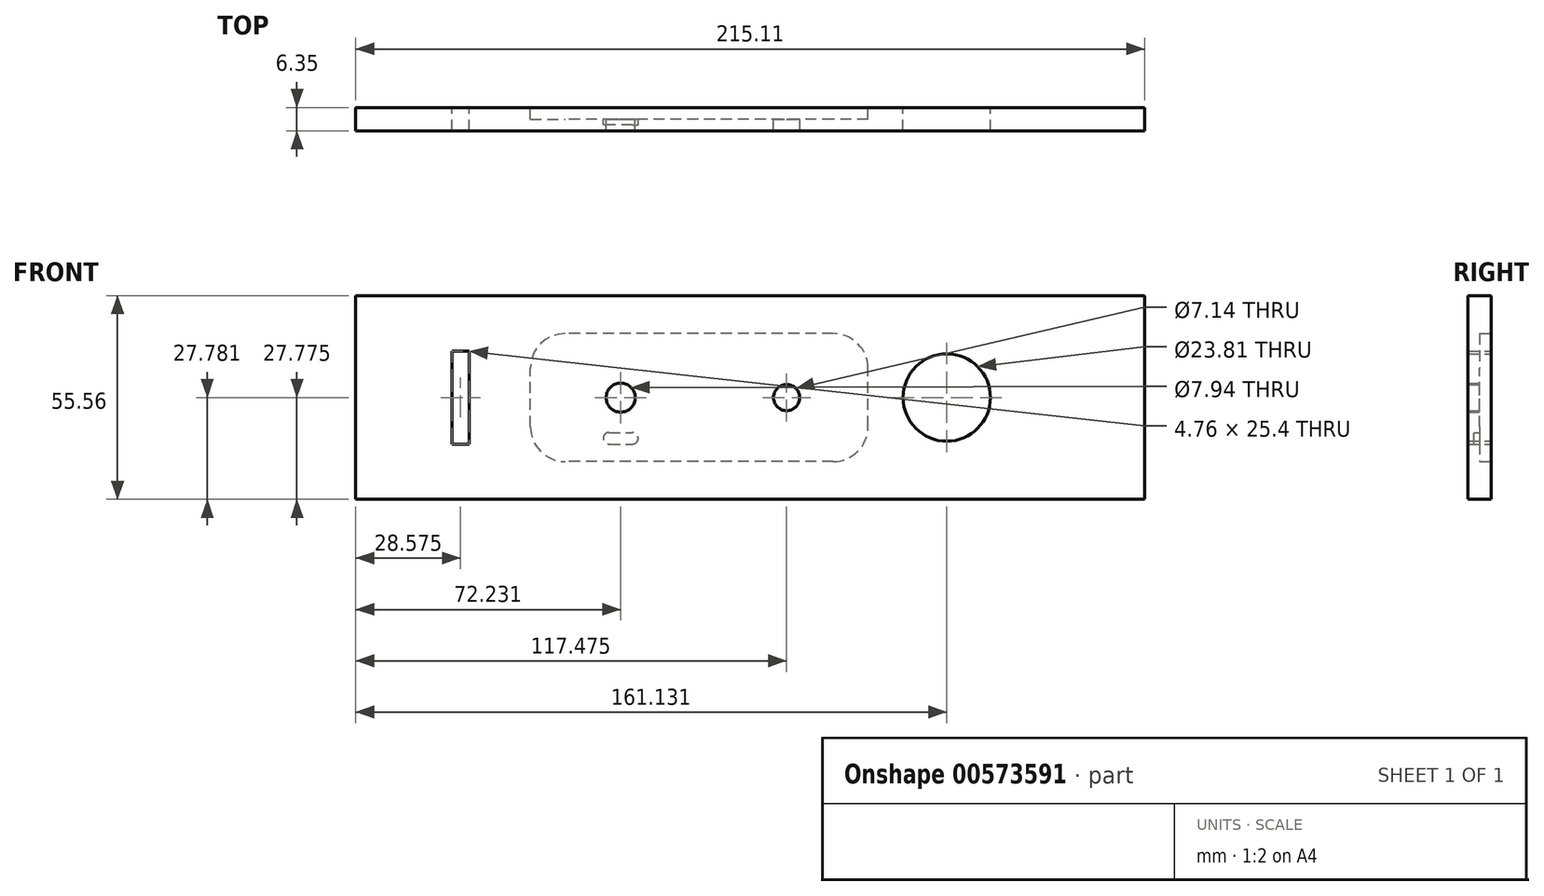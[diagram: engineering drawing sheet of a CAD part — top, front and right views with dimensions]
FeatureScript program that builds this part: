
annotation { "Feature Type Name" : "Feature", "Feature Type Description" : "" }
export const myFeature = defineFeature(function(context is Context, id is Id, definition is map)
    precondition{}
    {
        {
            var Q0;
            Q0=qCreatedBy(makeId("Front.planeOp"),FACE);
            var sketch = newSketch(context, id + "F0", { "sketchPlane" : qUnion([Q0])});
            skLineSegment(sketch, "E0.bottom", {"start": v(215.1, 55.56) * mm, "end": v(0, 55.56) * mm});
            skLineSegment(sketch, "E0.top", {"start": v(215.1, 0) * mm, "end": v(0, 0) * mm});
            skLineSegment(sketch, "E0.left", {"start": v(215.1, 55.56) * mm, "end": v(215.1, 0) * mm});
            skLineSegment(sketch, "E0.right", {"start": v(0, 55.56) * mm, "end": v(0, 0) * mm});
            skCircle(sketch, "E1", {"center": v(161.13, 27.78) * mm, "radius": 11.9 * mm});
            skCircle(sketch, "E2", {"center": v(117.48, 27.78) * mm, "radius": 3.57 * mm});
            skCircle(sketch, "E3", {"center": v(72.23, 27.77) * mm, "radius": 3.97 * mm});
            skSolve(sketch);
        }
        {
            var Q0;
            Q0 = qSketchRegion(id + "F0", true);
            extrude(context, id + "F1", {"entities" : qUnion([Q0]), "depth" : 6.35 * mm, "offsetDistance" : 25.4 * mm});
        }
        {
            var Q0;
            Q0=makeQuery(id+"F1.opExtrude","CAP_FACE",FACE,{"disambiguationData":[OSD([sQuery(id+"F0.wireOp",EDGE,"E0.bottom"),sQuery(id+"F0.wireOp",EDGE,"E0.top"),sQuery(id+"F0.wireOp",EDGE,"E0.left"),sQuery(id+"F0.wireOp",EDGE,"E0.right"),sQuery(id+"F0.wireOp",EDGE,"E1"),sQuery(id+"F0.wireOp",EDGE,"E2"),sQuery(id+"F0.wireOp",EDGE,"E3")])],"isStart":false});
            var sketch = newSketch(context, id + "F2", { "sketchPlane" : qUnion([Q0])});
            skLineSegment(sketch, "E4.bottom", {"start": v(26.2, 15.08) * mm, "end": v(30.96, 15.08) * mm});
            skLineSegment(sketch, "E4.top", {"start": v(26.2, 40.48) * mm, "end": v(30.96, 40.48) * mm});
            skLineSegment(sketch, "E4.left", {"start": v(26.2, 15.08) * mm, "end": v(26.2, 40.48) * mm});
            skLineSegment(sketch, "E4.right", {"start": v(30.96, 15.08) * mm, "end": v(30.96, 40.48) * mm});
            skSolve(sketch);
        }
        {
            var Q0;
            Q0 = qSketchRegion(id + "F2", true);
            extrude(context, id + "F3", {"entities" : qUnion([Q0]), "operationType" : NewBodyOperationType.REMOVE, "endBound" : BoundingType.THROUGH_ALL, "depth" : 25.4 * mm, "offsetDistance" : 25.4 * mm, "hasSecondDirection" : true, "secondDirectionBound" : SecondDirectionBoundingType.THROUGH_ALL, "secondDirectionOppositeDirection" : true, "secondDirectionDepth" : 25.4 * mm});
        }
        {
            var Q0;
            Q0=makeQuery(id+"F0.imprint","IMPRINT",FACE,{"disambiguationData":[TD([[makeQuery(id+"F0.imprint","IMPRINT",EDGE,{"derivedFrom":sQuery(id+"F0.wireOp",EDGE,"E0.bottom")}),1.0]])]});
            var sketch = newSketch(context, id + "F4", { "sketchPlane" : qUnion([Q0])});
            skLineSegment(sketch, "E5.bottom", {"start": v(130.18, 10.31) * mm, "end": v(57.15, 10.31) * mm});
            skLineSegment(sketch, "E5.top", {"start": v(130.18, 45.24) * mm, "end": v(57.15, 45.24) * mm});
            skLineSegment(sketch, "E5.left", {"start": v(139.7, 19.84) * mm, "end": v(139.7, 35.71) * mm});
            skLineSegment(sketch, "E5.right", {"start": v(47.63, 19.84) * mm, "end": v(47.63, 35.71) * mm});
            skPoint(sketch, "E6.visualSharp", {"position": v(139.7, 45.24) * mm});
            skArc(sketch, "E6.filletArc", {"start": v(139.7, 35.71) * mm, "mid": v(136.91, 42.45) * mm, "end": v(130.18, 45.24) * mm});
            skPoint(sketch, "E7.visualSharp", {"position": v(139.7, 10.31) * mm});
            skArc(sketch, "E7.filletArc", {"start": v(130.18, 10.31) * mm, "mid": v(136.91, 13.1) * mm, "end": v(139.7, 19.84) * mm});
            skPoint(sketch, "E8.visualSharp", {"position": v(47.63, 10.31) * mm});
            skArc(sketch, "E8.filletArc", {"start": v(47.63, 19.84) * mm, "mid": v(50.41, 13.1) * mm, "end": v(57.15, 10.31) * mm});
            skPoint(sketch, "E9.visualSharp", {"position": v(47.63, 45.24) * mm});
            skArc(sketch, "E9.filletArc", {"start": v(57.15, 45.24) * mm, "mid": v(50.41, 42.45) * mm, "end": v(47.63, 35.71) * mm});
            skSolve(sketch);
        }
        {
            var Q0;
            Q0 = qSketchRegion(id + "F4", true);
            extrude(context, id + "F5", {"entities" : qUnion([Q0]), "operationType" : NewBodyOperationType.REMOVE, "depth" : 3.17 * mm, "offsetDistance" : 25.4 * mm});
        }
        {
            var Q0;
            Q0=makeQuery(id+"F0.imprint","IMPRINT",FACE,{"disambiguationData":[TD([[makeQuery(id+"F0.imprint","IMPRINT",EDGE,{"derivedFrom":sQuery(id+"F0.wireOp",EDGE,"E0.bottom")}),1.0]])]});
            var sketch = newSketch(context, id + "F6", { "sketchPlane" : qUnion([Q0])});
            skLineSegment(sketch, "E10.bottom", {"start": v(75.4, 15.07) * mm, "end": v(69.06, 15.07) * mm});
            skLineSegment(sketch, "E10.top", {"start": v(75.4, 18.25) * mm, "end": v(69.06, 18.25) * mm});
            skArc(sketch, "E11", {"start": v(75.4, 15.07) * mm, "mid": v(77, 16.66) * mm, "end": v(75.4, 18.25) * mm});
            skArc(sketch, "E12", {"start": v(69.06, 18.25) * mm, "mid": v(67.47, 16.66) * mm, "end": v(69.06, 15.07) * mm});
            skSolve(sketch);
        }
        {
            var Q0;
            Q0 = qSketchRegion(id + "F6", true);
            extrude(context, id + "F7", {"entities" : qUnion([Q0]), "operationType" : NewBodyOperationType.REMOVE, "depth" : 4.76 * mm, "offsetDistance" : 25.4 * mm, "hasSecondDirection" : true, "secondDirectionOppositeDirection" : true, "secondDirectionDepth" : 3.17 * mm});
        }
    });
